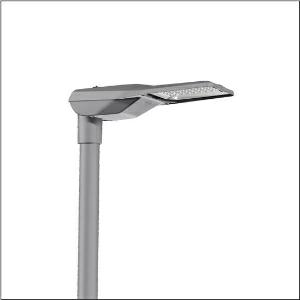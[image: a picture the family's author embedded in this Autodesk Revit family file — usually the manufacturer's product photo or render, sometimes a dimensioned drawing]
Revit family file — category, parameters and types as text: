
# Revit family: streetlight_sl_21_iq_mini___st1_0ab_5xe2m31v08gb_27e0
name_source: partatom
category: Lighting Fixtures
units: mm (PartAtom-declared; Revit-internal decimal feet)

## family parameters
Cut with Voids When Loaded = No
Host = Face
Light Source = No
Part Type = Normal
Room Calculation Point = No
Round Connector Dimension = Use Diameter
Shared = No

## types (1)
- --- (1 x LED, 5270 lm, 39.8 W, 3000K)
    Apparent Load = 40 VA
    CIE Flux Codes = 38 73 97 100 100
    Color Rendering = 70
    Color Temperature = 3000K
    Default Elevation = 1800 mm
    Description = Streetlight SL 21 iQ mini, mast luminaire, primary light control with lens, of PMMA, primary optical cover: cover, of toughened safety glass, transparent, light distribution: ST1.0aB, light emission: direct distribution, primary light characteristic: asymmetric, installation type: post-top, side-entry, LED, High Power LED, rated luminous flux: 5.270lm, luminous efficacy: 132lm/W, light colour: 730, colour temperature: 3000K, control: pre-setting: logarithmic dimming characteristic, Street-Remote, Auto-Match, Temp-Guard, Lumen-Switch, Night-Set, Smart-Wire, Light-Fading, Desk-Remote (wireless, voltage-free reading and setting of iQ features in the workshop via application-optimized NFC function/RFID function), optimised constant luminous flux control (CLO 2.0), mains connection: 220..240V, AC, 50/60Hz, start of lifetime: 40W, end of service life: 41W, reduction: 18W, luminaire housing, of diecast aluminium, powder-coated, Siteco® metallic grey (DB 702S), corrosivity category C5 mid according to DIN EN ISO 12944, please order mast flange separately, inclination adjustable: 0°, 5°, 10°, 15°, sealing non-destructively replaceable, multi-level sealing system, length: 628mm, width: 235mm, height: 110mm, mast flange for spigot size: 42mm (side-entry): 5XC10008XM4, 60/48mm (side-entry/post-top): 5XC10108XM2, 76/60mm (side-entry/post-top): 5XC10108XM1, Smart Interface above, protection rating (complete): IP66, insulation class (complete): insulation class II (safety insulation), certification: CE, ENEC, ENEC+, VDE, impact resistance: IK09, permissible operating ambient temperature for outdoor applications: -40..+50°C, standard-compliant lighting for roads and squares, packaging unit: 1 piece

Light Distribution: ST1.0aB
    Height = 110 mm
    Lamp = 1 x LED
    Lamp Light Flux = 5270 lm
    Lamp Power = 39.8 W
    Lamp count = 1
    Length = 625 mm
    Luminous efficacy = 132 lm/W
    Manufacturer = Siteco
    ModVariant = No
    Model = 5XE2M31V08GB
    Number of Poles = 1
    OnlyDefault = Yes
    Power Factor = 1
    Product Name = Streetlight SL 21 iQ mini | ST1.0aB
    Product group = mast luminaire | pylon top
    ProductGroupID = 6100
    Protection Class = Protection class II
    Protection Degree = IP 66
    RLX_Detail_Level = 1
    RLX_Emergency_Light_Flux = 0 lm
    RLX_Emergency_Type = 0
    RLX_Emergency_Type_DB = No
    RlxData = <blob elided: 92829 chars, md5=3cd0804b>
    Socket = socket
    Standby Power = 0 W
    System Light Flux = 5270 lm
    System Power = 40 W
    Type Comments = factory setting: luminous flux: 100 % | dim-lin: 254 | 800 mA
    Type Image = l_1003515.jpg
    URL = http://relux.com
    VarID = @adj_081363
    Voltage = 0 V
    Weight = 0.00 kg
    Width = 234 mm

## geometry (parser evidence)
native form markers: Blend x4, Sweep x12
no freeform markers — native parametric forms only
